# Revit family: RDI2
name_source: partatom
category: Lighting Fixtures
units: mm (PartAtom-declared; Revit-internal decimal feet)

## family parameters
Cut with Voids When Loaded = No
Host = Face
Light Source = Yes
OmniClass Number = 23.80.70.11
OmniClass Title = Luminaries for Internal Lighting
Part Type = Normal
Room Calculation Point = No
Round Connector Dimension = Use Diameter
Shared = No

## types (1)
- RDI2
    Color Filter = 16777215
    Default Elevation = 48"
    Description = Mid sized architectural wallpacks in three stylish shapes with molded contours to accentuate building architecture. Provides excellent illumination in energy-saving LED systems.
    Dimming Lamp Color Temperature Shift = <None>
    Finish = Black
    Finish2 = White
    Lamp = LED
    Manufacturer = EXO
    Model = RDI2
    Opal lens = Glass - White
    Photometric Web File = TRP2-24L-30-3K7-1.ies
    Tilt Angle = 70.00°
    URL = https://www.currentlighting.com
    Wattage Comments = 30W

## geometry (parser evidence)
native form markers: Blend x2, Sweep x1
no freeform markers — native parametric forms only
